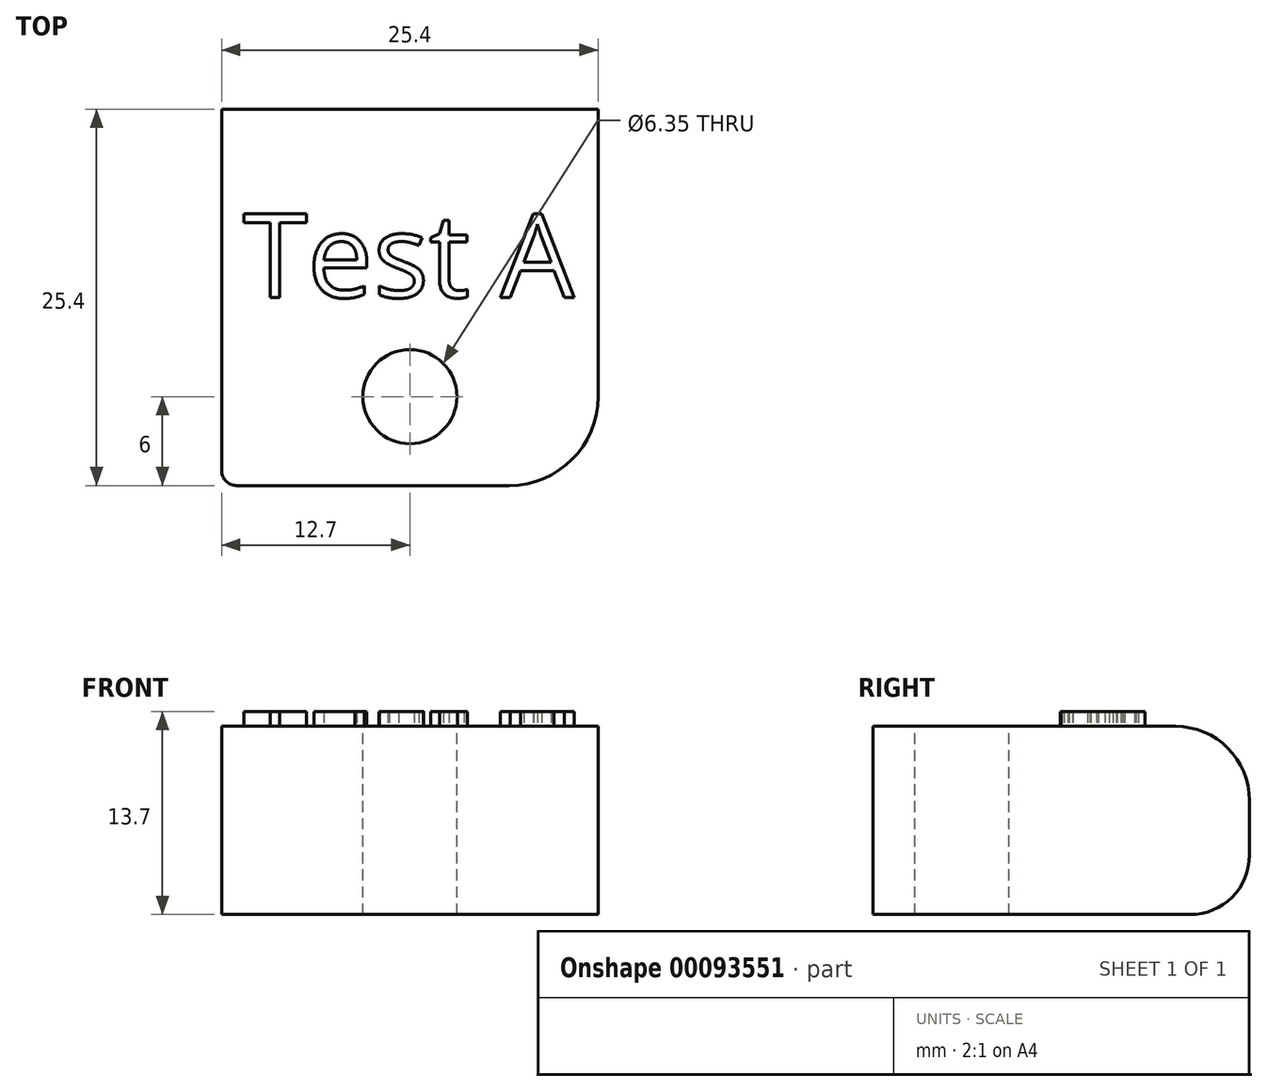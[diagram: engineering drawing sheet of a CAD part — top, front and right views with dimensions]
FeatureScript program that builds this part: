
annotation { "Feature Type Name" : "Feature", "Feature Type Description" : "" }
export const myFeature = defineFeature(function(context is Context, id is Id, definition is map)
    precondition{}
    {
        {
            var Q0;
            Q0=qCreatedBy(makeId("Top.planeOp"),FACE);
            var sketch = newSketch(context, id + "F0", { "sketchPlane" : qUnion([Q0])});
            skLineSegment(sketch, "E0.bottom", {"start": v(12.7, 12.7) * mm, "end": v(-12.7, 12.7) * mm});
            skLineSegment(sketch, "E0.top", {"start": v(12.7, -12.7) * mm, "end": v(-12.7, -12.7) * mm});
            skLineSegment(sketch, "E0.left", {"start": v(12.7, 12.7) * mm, "end": v(12.7, -12.7) * mm});
            skLineSegment(sketch, "E0.right", {"start": v(-12.7, 12.7) * mm, "end": v(-12.7, -12.7) * mm});
            skPoint(sketch, "E0.middle", {"position": v(0, 0) * mm});
            skSolve(sketch);
        }
        {
            var Q0;
            Q0 = qSketchRegion(id + "F0", true);
            extrude(context, id + "F1", {"entities" : qUnion([Q0]), "depth" : 12.7 * mm});
        }
        {
            var Q0;
            Q0=makeQuery(id+"F1.opExtrude","CAP_FACE",FACE,{"disambiguationData":[OSD([sQuery(id+"F0.wireOp",EDGE,"E0.bottom"),sQuery(id+"F0.wireOp",EDGE,"E0.top"),sQuery(id+"F0.wireOp",EDGE,"E0.left"),sQuery(id+"F0.wireOp",EDGE,"E0.right")])],"isStart":false});
            var sketch = newSketch(context, id + "F2", { "sketchPlane" : qUnion([Q0])});
            skCircle(sketch, "E1", {"center": v(0, -6.7) * mm, "radius": 3.17 * mm});
            skSolve(sketch);
        }
        {
            var Q0;
            Q0 = qSketchRegion(id + "F2", true);
            extrude(context, id + "F3", {"entities" : qUnion([Q0]), "operationType" : NewBodyOperationType.REMOVE, "endBound" : BoundingType.THROUGH_ALL, "oppositeDirection" : true, "depth" : 25 * mm});
        }
        {
            var Q0;
            Q0=makeQuery(id+"F1.opExtrude","SWEPT_EDGE",EDGE,{"disambiguationData":[OSD([sQuery(id+"F0.wireOp",EDGE,"E0.top"),sQuery(id+"F0.wireOp",EDGE,"E0.left")])]});
            fillet(context, id + "F4", {"entities" : qUnion([Q0]), "radius" : 6 * mm, "tangentPropagation" : true, "allowEdgeOverflow" : false});
        }
        {
            var Q0;
            Q0=makeQuery(id+"F1.opExtrude","SWEPT_EDGE",EDGE,{"disambiguationData":[OSD([sQuery(id+"F0.wireOp",EDGE,"E0.top"),sQuery(id+"F0.wireOp",EDGE,"E0.right")])]});
            fillet(context, id + "F5", {"entities" : qUnion([Q0]), "radius" : 1 * mm, "tangentPropagation" : true, "allowEdgeOverflow" : false});
        }
        {
            var Q0;
            Q0=makeQuery(id+"F1.opExtrude","CAP_EDGE",EDGE,{"disambiguationData":[OSD([sQuery(id+"F0.wireOp",EDGE,"E0.bottom")])],"isStart":false});
            fillet(context, id + "F6", {"entities" : qUnion([Q0]), "radius" : 5 * mm, "tangentPropagation" : true, "allowEdgeOverflow" : false});
        }
        {
            var Q0;
            Q0=makeQuery(id+"F1.opExtrude","CAP_EDGE",EDGE,{"disambiguationData":[OSD([sQuery(id+"F0.wireOp",EDGE,"E0.bottom")])],"isStart":true});
            fillet(context, id + "F7", {"entities" : qUnion([Q0]), "radius" : 4 * mm, "tangentPropagation" : true, "allowEdgeOverflow" : false});
        }
        {
            var Q0;
            Q0=makeQuery(id+"F1.opExtrude","CAP_FACE",FACE,{"disambiguationData":[OSD([sQuery(id+"F0.wireOp",EDGE,"E0.bottom"),sQuery(id+"F0.wireOp",EDGE,"E0.top"),sQuery(id+"F0.wireOp",EDGE,"E0.left"),sQuery(id+"F0.wireOp",EDGE,"E0.right")])],"isStart":false});
            var sketch = newSketch(context, id + "F8", { "sketchPlane" : qUnion([Q0])});
            skLineSegment(sketch, "E2", {"start": v(-12.7, 0) * mm, "end": v(12.7, 0) * mm, "construction": true});
            skText(sketch, "E3", { "text": "Test A", "fontName": "OpenSans-Regular.ttf"});
            const initialGuessF8  = {"E3": [-0.01128, 0, 1, 0, 0.00568]};
            skSetInitialGuess(sketch, initialGuessF8);
            skSolve(sketch);
        }
        {
            var Q0;
            Q0 = qSketchRegion(id + "F8", true);
            extrude(context, id + "F9", {"entities" : qUnion([Q0]), "operationType" : NewBodyOperationType.ADD, "depth" : 1 * mm});
        }
    });
